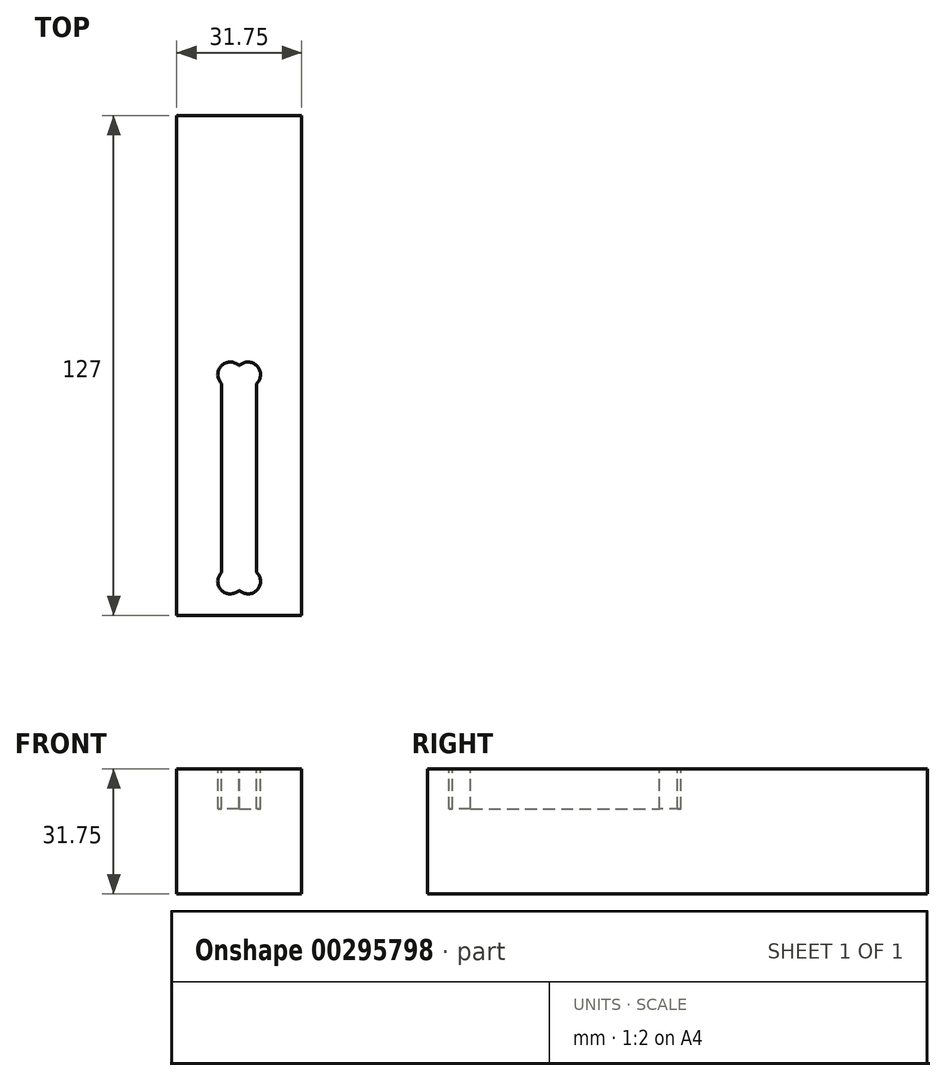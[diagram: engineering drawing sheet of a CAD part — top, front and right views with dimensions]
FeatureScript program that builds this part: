
annotation { "Feature Type Name" : "Feature", "Feature Type Description" : "" }
export const myFeature = defineFeature(function(context is Context, id is Id, definition is map)
    precondition{}
    {
        {
            var Q0;
            Q0=qCreatedBy(makeId("Top.planeOp"),FACE);
            var sketch = newSketch(context, id + "F0", { "sketchPlane" : qUnion([Q0])});
            skLineSegment(sketch, "E0.bottom", {"start": v(0, 0) * mm, "end": v(31.75, 0) * mm});
            skLineSegment(sketch, "E0.top", {"start": v(0, 127) * mm, "end": v(31.75, 127) * mm});
            skLineSegment(sketch, "E0.left", {"start": v(0, 0) * mm, "end": v(0, 127) * mm});
            skLineSegment(sketch, "E0.right", {"start": v(31.75, 0) * mm, "end": v(31.75, 127) * mm});
            skSolve(sketch);
        }
        {
            var Q0;
            Q0 = qSketchRegion(id + "F0", true);
            extrude(context, id + "F1", {"entities" : qUnion([Q0]), "depth" : 31.75 * mm});
        }
        {
            var Q0;
            Q0=makeQuery(id+"F1.opExtrude","CAP_FACE",FACE,{"disambiguationData":[OSD([sQuery(id+"F0.wireOp",EDGE,"E0.bottom"),sQuery(id+"F0.wireOp",EDGE,"E0.top"),sQuery(id+"F0.wireOp",EDGE,"E0.left"),sQuery(id+"F0.wireOp",EDGE,"E0.right")])],"isStart":false});
            var sketch = newSketch(context, id + "F2", { "sketchPlane" : qUnion([Q0])});
            skLineSegment(sketch, "E1", {"start": v(15.88, 0) * mm, "end": v(15.88, 83.15) * mm, "construction": true});
            skLineSegment(sketch, "E2.bottom", {"start": v(20.32, 6.35) * mm, "end": v(11.43, 6.35) * mm});
            skLineSegment(sketch, "E2.top", {"start": v(20.32, 63.5) * mm, "end": v(11.43, 63.5) * mm});
            skLineSegment(sketch, "E2.left", {"start": v(20.32, 6.35) * mm, "end": v(20.32, 63.5) * mm});
            skLineSegment(sketch, "E2.right", {"start": v(11.43, 6.35) * mm, "end": v(11.43, 63.5) * mm});
            skPoint(sketch, "E2.middle", {"position": v(15.88, 34.93) * mm});
            skSolve(sketch);
        }
        {
            var Q0;
            Q0 = qSketchRegion(id + "F2", true);
            extrude(context, id + "F3", {"entities" : qUnion([Q0]), "operationType" : NewBodyOperationType.REMOVE, "oppositeDirection" : true, "depth" : 10.16 * mm});
        }
        {
            var Q0;
            Q0=makeQuery(id+"F1.opExtrude","CAP_FACE",FACE,{"disambiguationData":[OSD([sQuery(id+"F0.wireOp",EDGE,"E0.bottom"),sQuery(id+"F0.wireOp",EDGE,"E0.top"),sQuery(id+"F0.wireOp",EDGE,"E0.left"),sQuery(id+"F0.wireOp",EDGE,"E0.right")])],"isStart":false});
            var sketch = newSketch(context, id + "F4", { "sketchPlane" : qUnion([Q0])});
            skCircle(sketch, "E3", {"center": v(18.13, 61.2) * mm, "radius": 3.18 * mm});
            skLineSegment(sketch, "E4", {"start": v(15.87, 6.35) * mm, "end": v(15.87, 63.43) * mm, "construction": true});
            skLineSegment(sketch, "E5", {"start": v(20.32, 34.93) * mm, "end": v(11.43, 34.93) * mm, "construction": true});
            skCircle(sketch, "E6.MirrorC", {"center": v(18.13, 8.65) * mm, "radius": 3.18 * mm});
            skCircle(sketch, "E7.MirrorC", {"center": v(13.62, 8.65) * mm, "radius": 3.18 * mm});
            skCircle(sketch, "E8.MirrorC", {"center": v(13.62, 61.2) * mm, "radius": 3.18 * mm});
            skSolve(sketch);
        }
        {
            var Q0;
            Q0 = qSketchRegion(id + "F4", true);
            var Q1;
            Q1=makeQuery(id+"F3.boolean.opBoolean","COPY",FACE,{"derivedFrom":makeQuery(id+"F3.opExtrude","CAP_FACE",FACE,{"disambiguationData":[OSD([sQuery(id+"F2.wireOp",EDGE,"E2.bottom"),sQuery(id+"F2.wireOp",EDGE,"E2.top"),sQuery(id+"F2.wireOp",EDGE,"E2.left"),sQuery(id+"F2.wireOp",EDGE,"E2.right")])],"isStart":false})});
            extrude(context, id + "F5", {"entities" : qUnion([Q0]), "operationType" : NewBodyOperationType.REMOVE, "endBound" : BoundingType.UP_TO_SURFACE, "oppositeDirection" : true, "endBoundEntityFace" : qUnion([Q1]), "depth" : 25.4 * mm});
        }
    });
